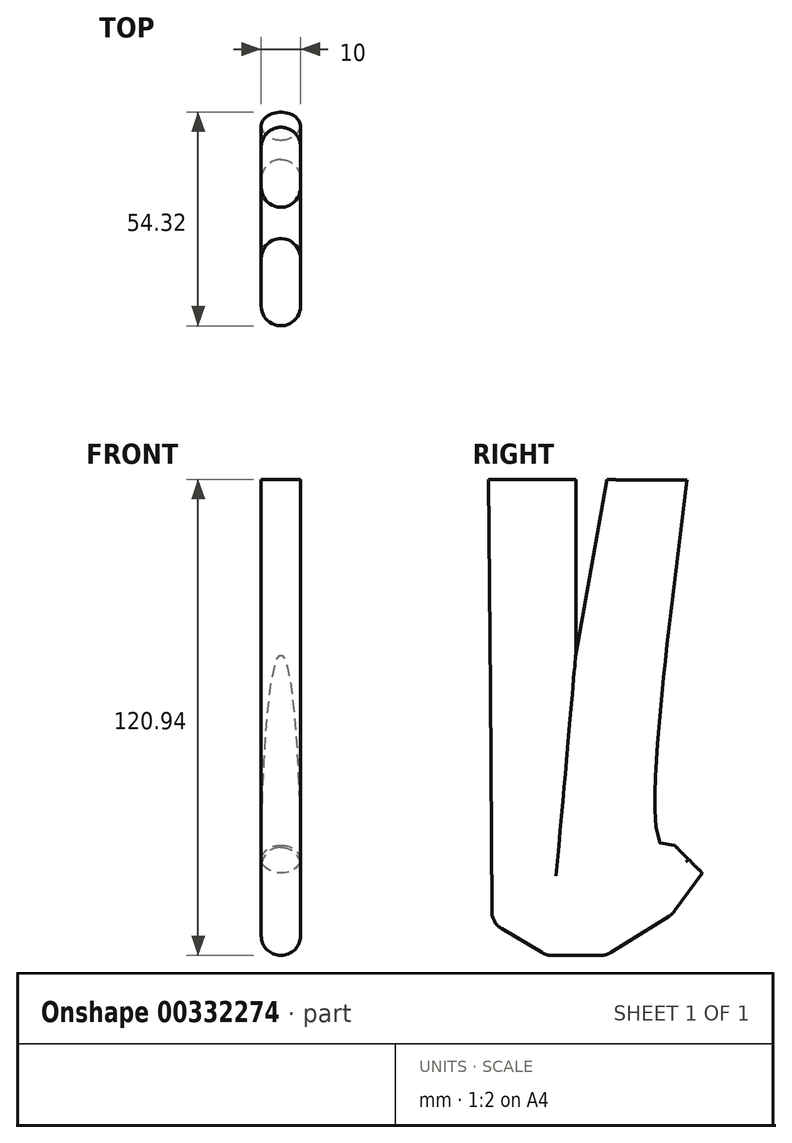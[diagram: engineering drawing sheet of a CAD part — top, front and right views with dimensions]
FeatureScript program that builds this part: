
annotation { "Feature Type Name" : "Feature", "Feature Type Description" : "" }
export const myFeature = defineFeature(function(context is Context, id is Id, definition is map)
    precondition{}
    {
        {
            var Q0;
            Q0=qCreatedBy(makeId("Top.planeOp"),FACE);
            var sketch = newSketch(context, id + "F0", { "sketchPlane" : qUnion([Q0])});
            skLineSegment(sketch, "E0.bottom", {"start": v(50, 50) * mm, "end": v(-50, 50) * mm});
            skLineSegment(sketch, "E0.top", {"start": v(50, -50) * mm, "end": v(-50, -50) * mm});
            skLineSegment(sketch, "E0.left", {"start": v(50, 50) * mm, "end": v(50, -50) * mm});
            skLineSegment(sketch, "E0.right", {"start": v(-50, 50) * mm, "end": v(-50, -50) * mm});
            skPoint(sketch, "E0.middle", {"position": v(0, 0) * mm});
            skSolve(sketch);
        }
        {
            var Q0;
            Q0=qCreatedBy(makeId("Right.planeOp"),FACE);
            var sketch = newSketch(context, id + "F1", { "sketchPlane" : qUnion([Q0])});
            skLineSegment(sketch, "E1", {"start": v(32.93, -92.93) * mm, "end": v(40, -100) * mm});
            skLineSegment(sketch, "E2", {"start": v(40, -100) * mm, "end": v(50, -100) * mm});
            skLineSegment(sketch, "E3", {"start": v(50, -100) * mm, "end": v(50, 0) * mm});
            skLineSegment(sketch, "E4", {"start": v(40, -100) * mm, "end": v(32.42, -110.44) * mm});
            skLineSegment(sketch, "E5", {"start": v(32.42, -110.44) * mm, "end": v(15.56, -120.94) * mm});
            skLineSegment(sketch, "E6", {"start": v(15.56, -120.94) * mm, "end": v(0.42, -120.94) * mm});
            skLineSegment(sketch, "E7", {"start": v(0.42, -120.94) * mm, "end": v(-13.45, -112.58) * mm});
            skLineSegment(sketch, "E8", {"start": v(-13.45, -112.58) * mm, "end": v(-13.84, -53.79) * mm});
            skLineSegment(sketch, "E9", {"start": v(15.79, -0.07) * mm, "end": v(7.9, -44.29) * mm});
            skLineSegment(sketch, "E10", {"start": v(7.9, -44.29) * mm, "end": v(7.9, -0.07) * mm});
            skLineSegment(sketch, "E11", {"start": v(7.9, -0.07) * mm, "end": v(-14.32, 0) * mm});
            skLineSegment(sketch, "E12", {"start": v(-14.32, 0) * mm, "end": v(-13.84, -53.79) * mm});
            skLineSegment(sketch, "E13", {"start": v(15.79, -0.07) * mm, "end": v(36.15, -0.14) * mm});
            skFitSpline(sketch, "E14", {"points": [v(32.93, -92.93) * mm, v(29.65, -92.93) * mm, v(36.15, -0.14) * mm], "startDerivative": vector(-23, -8.71) * mm, "endDerivative": vector(19.71, 156.62) * mm});
            skSolve(sketch);
        }
        {
            var Q0;
            Q0=makeQuery(id+"F1.imprint","IMPRINT",FACE,{"disambiguationData":[TD([[makeQuery(id+"F1.imprint","IMPRINT",EDGE,{"derivedFrom":sQuery(id+"F1.wireOp",EDGE,"E1")}),-1.0]])]});
            extrude(context, id + "F2", {"entities" : qUnion([Q0]), "endBound" : BoundingType.SYMMETRIC, "depth" : 10 * mm});
        }
        {
            var Q0;
            Q0=makeQuery(id+"F2.opExtrude","CAP_EDGE",EDGE,{"disambiguationData":[OSD([sQuery(id+"F1.wireOp",EDGE,"E8")])],"isStart":false});
            var Q1;
            Q1=makeQuery(id+"F2.opExtrude","CAP_EDGE",EDGE,{"disambiguationData":[OSD([sQuery(id+"F1.wireOp",EDGE,"E7")])],"isStart":false});
            var Q2;
            Q2=makeQuery(id+"F2.opExtrude","CAP_EDGE",EDGE,{"disambiguationData":[OSD([sQuery(id+"F1.wireOp",EDGE,"E6")])],"isStart":false});
            var Q3;
            Q3=makeQuery(id+"F2.opExtrude","CAP_EDGE",EDGE,{"disambiguationData":[OSD([sQuery(id+"F1.wireOp",EDGE,"E5")])],"isStart":false});
            var Q4;
            Q4=makeQuery(id+"F2.opExtrude","CAP_EDGE",EDGE,{"disambiguationData":[OSD([sQuery(id+"F1.wireOp",EDGE,"E4")])],"isStart":false});
            var Q5;
            Q5=makeQuery(id+"F2.opExtrude","CAP_EDGE",EDGE,{"disambiguationData":[OSD([sQuery(id+"F1.wireOp",EDGE,"49eb233f-eca1-4608-b86e-9a41fd80e5eb")])],"isStart":false});
            var Q6;
            Q6=makeQuery(id+"F2.opExtrude","CAP_EDGE",EDGE,{"disambiguationData":[OSD([sQuery(id+"F1.wireOp",EDGE,"zjXfg7Vx-LYZx-WJwB-u50H-vYy3XpUTTi9i")])],"isStart":false});
            var Q7;
            Q7=makeQuery(id+"F2.opExtrude","CAP_EDGE",EDGE,{"disambiguationData":[OSD([sQuery(id+"F1.wireOp",EDGE,"E5")])],"isStart":true});
            var Q8;
            Q8=makeQuery(id+"F2.opExtrude","CAP_EDGE",EDGE,{"disambiguationData":[OSD([sQuery(id+"F1.wireOp",EDGE,"E6")])],"isStart":true});
            var Q9;
            Q9=makeQuery(id+"F2.opExtrude","CAP_EDGE",EDGE,{"disambiguationData":[OSD([sQuery(id+"F1.wireOp",EDGE,"E7")])],"isStart":true});
            var Q10;
            Q10=makeQuery(id+"F2.opExtrude","CAP_EDGE",EDGE,{"disambiguationData":[OSD([sQuery(id+"F1.wireOp",EDGE,"E4")])],"isStart":true});
            var Q11;
            Q11=makeQuery(id+"F2.opExtrude","CAP_EDGE",EDGE,{"disambiguationData":[OSD([sQuery(id+"F1.wireOp",EDGE,"49eb233f-eca1-4608-b86e-9a41fd80e5eb")])],"isStart":true});
            var Q12;
            Q12=makeQuery(id+"F2.opExtrude","CAP_EDGE",EDGE,{"disambiguationData":[OSD([sQuery(id+"F1.wireOp",EDGE,"E8")])],"isStart":true});
            var Q13;
            Q13=makeQuery(id+"F2.opExtrude","CAP_EDGE",EDGE,{"disambiguationData":[OSD([sQuery(id+"F1.wireOp",EDGE,"zjXfg7Vx-LYZx-WJwB-u50H-vYy3XpUTTi9i")])],"isStart":true});
            var Q14;
            Q14=makeQuery(id+"F2.opExtrude","SWEPT_FACE",FACE,{"disambiguationData":[OSD([sQuery(id+"F1.wireOp",EDGE,"E5")])]});
            var Q15;
            Q15=makeQuery(id+"F2.opExtrude","SWEPT_EDGE",EDGE,{"disambiguationData":[OSD([sQuery(id+"F1.wireOp",EDGE,"E6"),sQuery(id+"F1.wireOp",EDGE,"E7")])]});
            var Q16;
            Q16=makeQuery(id+"F2.opExtrude","SWEPT_EDGE",EDGE,{"disambiguationData":[OSD([sQuery(id+"F1.wireOp",EDGE,"E7"),sQuery(id+"F1.wireOp",EDGE,"E8")])]});
            var Q17;
            Q17=makeQuery(id+"F2.opExtrude","CAP_EDGE",EDGE,{"disambiguationData":[OSD([sQuery(id+"F1.wireOp",EDGE,"44457354-6a0a-461b-9640-03c7e871ec64")])],"isStart":false});
            var Q18;
            Q18=makeQuery(id+"F2.opExtrude","CAP_EDGE",EDGE,{"disambiguationData":[OSD([sQuery(id+"F1.wireOp",EDGE,"IOLs24wW-nGt2-bCdK-CUzV-omeq2doUS0Fj")])],"isStart":false});
            var Q19;
            Q19=makeQuery(id+"F2.opExtrude","CAP_EDGE",EDGE,{"disambiguationData":[OSD([sQuery(id+"F1.wireOp",EDGE,"E10")])],"isStart":false});
            var Q20;
            Q20=makeQuery(id+"F2.opExtrude","CAP_EDGE",EDGE,{"disambiguationData":[OSD([sQuery(id+"F1.wireOp",EDGE,"E9")])],"isStart":false});
            var Q21;
            Q21=makeQuery(id+"F2.opExtrude","CAP_EDGE",EDGE,{"disambiguationData":[OSD([sQuery(id+"F1.wireOp",EDGE,"44457354-6a0a-461b-9640-03c7e871ec64")])],"isStart":true});
            var Q22;
            Q22=makeQuery(id+"F2.opExtrude","CAP_EDGE",EDGE,{"disambiguationData":[OSD([sQuery(id+"F1.wireOp",EDGE,"E10")])],"isStart":true});
            var Q23;
            Q23=makeQuery(id+"F2.opExtrude","CAP_EDGE",EDGE,{"disambiguationData":[OSD([sQuery(id+"F1.wireOp",EDGE,"E9")])],"isStart":true});
            var Q24;
            Q24=makeQuery(id+"F2.opExtrude","CAP_EDGE",EDGE,{"disambiguationData":[OSD([sQuery(id+"F1.wireOp",EDGE,"IOLs24wW-nGt2-bCdK-CUzV-omeq2doUS0Fj")])],"isStart":true});
            var Q25;
            Q25=makeQuery(id+"F2.opExtrude","CAP_EDGE",EDGE,{"disambiguationData":[OSD([sQuery(id+"F1.wireOp",EDGE,"1a2d0c1b-d173-4b5c-91dd-a013b25bc349")])],"isStart":true});
            var Q26;
            Q26=makeQuery(id+"F2.opExtrude","SWEPT_EDGE",EDGE,{"disambiguationData":[OSD([sQuery(id+"F1.wireOp",EDGE,"ctv6Uj9i-5GiC-c2g8-MQwH-dTNLdzQty9C9"),sQuery(id+"F1.wireOp",EDGE,"01453e82-e355-43f1-b94c-4e8e36261eb0")])]});
            var Q27;
            Q27=makeQuery(id+"F2.opExtrude","CAP_EDGE",EDGE,{"disambiguationData":[OSD([sQuery(id+"F1.wireOp",EDGE,"E14")])],"isStart":false});
            var Q28;
            Q28=makeQuery(id+"F2.opExtrude","CAP_EDGE",EDGE,{"disambiguationData":[OSD([sQuery(id+"F1.wireOp",EDGE,"E14")])],"isStart":true});
            fillet(context, id + "F3", {"entities" : qUnion([Q0, Q1, Q2, Q3, Q4, Q5, Q6, Q7, Q8, Q9, Q10, Q11, Q12, Q13, Q14, Q15, Q16, Q17, Q18, Q19, Q20, Q21, Q22, Q23, Q24, Q25, Q26, Q27, Q28]), "radius" : 5 * mm, "tangentPropagation" : true, "allowEdgeOverflow" : false});
        }
    });
